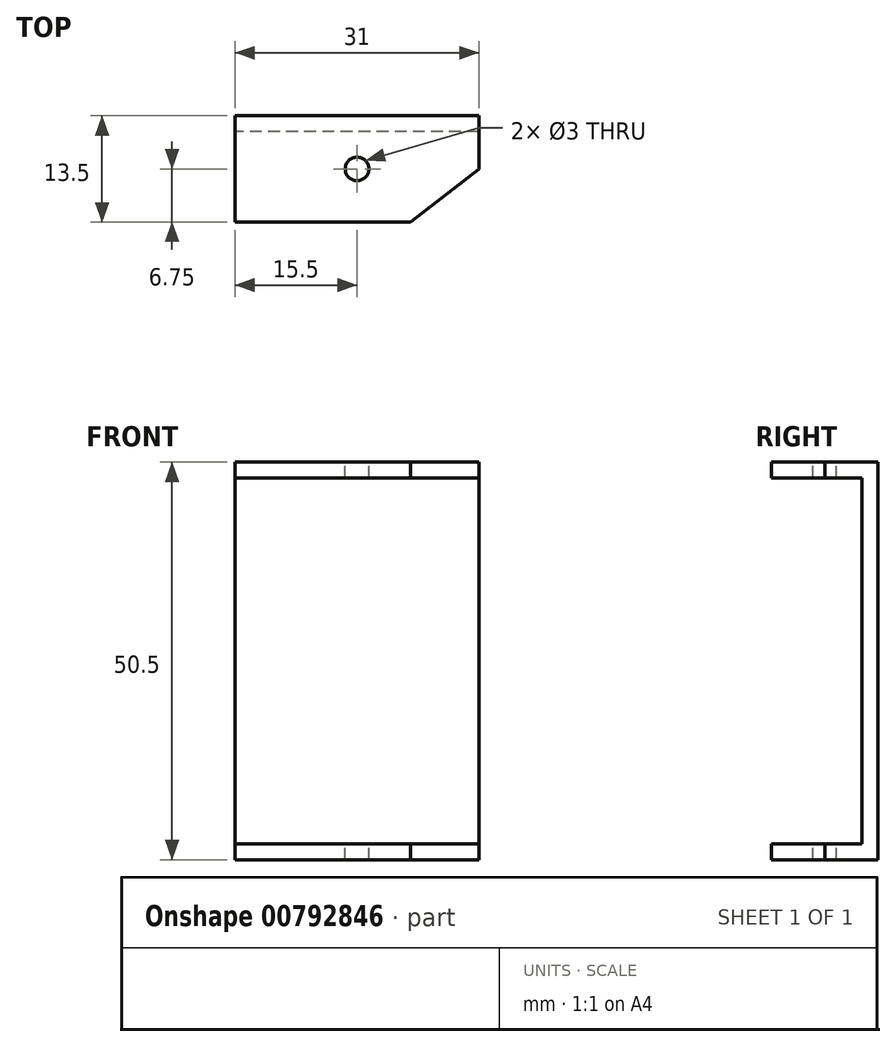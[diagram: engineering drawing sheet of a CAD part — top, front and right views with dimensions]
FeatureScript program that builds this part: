
annotation { "Feature Type Name" : "Feature", "Feature Type Description" : "" }
export const myFeature = defineFeature(function(context is Context, id is Id, definition is map)
    precondition{}
    {
        {
            var Q0;
            Q0=qCreatedBy(makeId("Right.planeOp"),FACE);
            var sketch = newSketch(context, id + "F0", { "sketchPlane" : qUnion([Q0])});
            skLineSegment(sketch, "E0", {"start": v(0, 7.56) * mm, "end": v(0, -38.94) * mm});
            skLineSegment(sketch, "E1", {"start": v(0, 7.56) * mm, "end": v(-11.5, 7.56) * mm});
            skLineSegment(sketch, "E2", {"start": v(0, -38.94) * mm, "end": v(-11.5, -38.94) * mm});
            skLineSegment(sketch, "E3", {"start": v(-11.5, -38.94) * mm, "end": v(-11.5, -40.94) * mm});
            skLineSegment(sketch, "E4", {"start": v(-11.5, 7.56) * mm, "end": v(-11.5, 9.56) * mm});
            skLineSegment(sketch, "E5", {"start": v(-11.5, 9.56) * mm, "end": v(2, 9.56) * mm});
            skLineSegment(sketch, "E6", {"start": v(2, 9.56) * mm, "end": v(2, -40.94) * mm});
            skLineSegment(sketch, "E7", {"start": v(2, -40.94) * mm, "end": v(-11.5, -40.94) * mm});
            skSolve(sketch);
        }
        {
            var Q0;
            Q0 = qSketchRegion(id + "F0", true);
            extrude(context, id + "F1", {"entities" : qUnion([Q0]), "depth" : 31 * mm, "offsetDistance" : 25 * mm});
        }
        {
            var Q0;
            Q0=makeQuery(id+"F1.opExtrude","SWEPT_FACE",FACE,{"disambiguationData":[OSD([sQuery(id+"F0.wireOp",EDGE,"E5")])]});
            var sketch = newSketch(context, id + "F2", { "sketchPlane" : qUnion([Q0])});
            skLineSegment(sketch, "E8", {"start": v(15.5, 6.89) * mm, "end": v(15.5, -21.26) * mm, "construction": true});
            skPoint(sketch, "E8.startSnap0", {"position": v(15.5, 2) * mm});
            skCircle(sketch, "E9", {"center": v(15.5, -4.75) * mm, "radius": 1.5 * mm});
            skPoint(sketch, "E9.centerSnap0", {"position": v(0, -4.75) * mm});
            skLineSegment(sketch, "E10", {"start": v(31, -11.5) * mm, "end": v(31, -4.75) * mm});
            skLineSegment(sketch, "E11", {"start": v(31, -4.75) * mm, "end": v(22.29, -11.5) * mm});
            skLineSegment(sketch, "E12", {"start": v(22.29, -11.5) * mm, "end": v(31, -11.5) * mm});
            skSolve(sketch);
        }
        {
            var Q0;
            Q0 = qSketchRegion(id + "F2", true);
            extrude(context, id + "F3", {"entities" : qUnion([Q0]), "operationType" : NewBodyOperationType.REMOVE, "oppositeDirection" : true, "depth" : 77 * mm, "offsetDistance" : 25 * mm});
        }
    });
